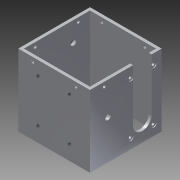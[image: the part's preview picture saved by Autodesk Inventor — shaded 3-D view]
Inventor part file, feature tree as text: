
AUTODESK INVENTOR PART (.ipt)
format: ipt  version: 2013 (Build 170138000, 138)  size: 199,680 bytes
history: native  units: mm
features: sketch x6, hole x5, thread x4, other x1, extrude x1
ambient origin geometry x1: Origin
feature tree (17):
  other  "ソリッド1"
  extrude  "押し出し1"  Depth=50.0mm
  hole  "穴1"  [1 undecoded]
  hole  "穴6"  [1 undecoded]
  hole  "穴13"  [1 undecoded]
  thread  "ねじ13"
  thread  "ねじ14"
  thread  "ねじ15"
  thread  "ねじ16"
  hole  "穴14"  [1 undecoded]
  hole  "穴15"  [1 undecoded]
  sketch  "スケッチ1"
  sketch  "スケッチ3"
  sketch  "スケッチ11"
  sketch  "スケッチ18"
  sketch  "スケッチ19"
  sketch  "スケッチ20"
note: 5 required parameter values undecoded (feature->parameter linkage not recoverable at this tier; creation-order binding heuristic only, values carry confidence <= 0.55)
